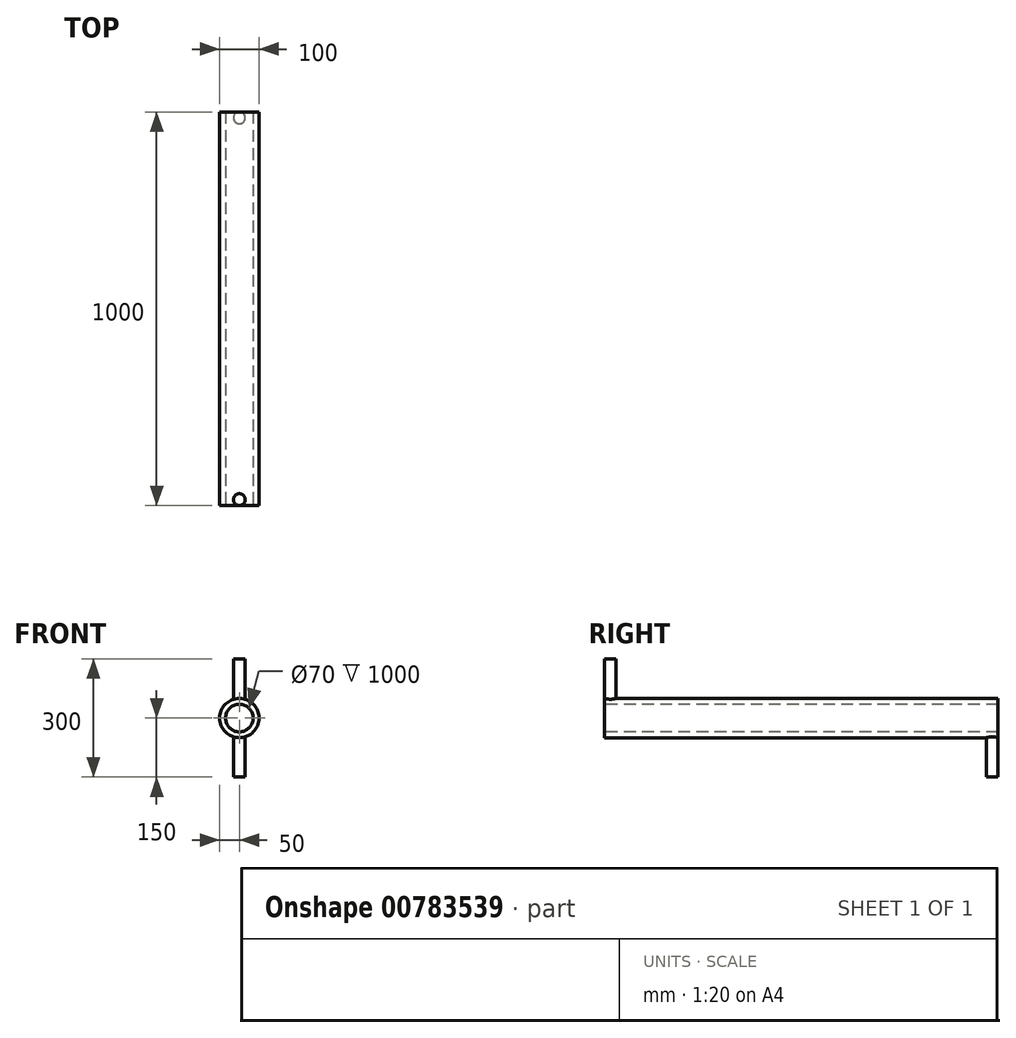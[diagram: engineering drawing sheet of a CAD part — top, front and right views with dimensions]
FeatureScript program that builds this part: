
annotation { "Feature Type Name" : "Feature", "Feature Type Description" : "" }
export const myFeature = defineFeature(function(context is Context, id is Id, definition is map)
    precondition{}
    {
        {
            var Q0;
            Q0=qCreatedBy(makeId("Front.planeOp"),FACE);
            var sketch = newSketch(context, id + "F0", { "sketchPlane" : qUnion([Q0])});
            skCircle(sketch, "E0", {"center": v(0, 0) * mm, "radius": 50 * mm});
            skCircle(sketch, "E1", {"center": v(0, 0) * mm, "radius": 35 * mm});
            skSolve(sketch);
        }
        {
            var Q0;
            Q0=makeQuery(id+"F0.imprint","IMPRINT",FACE,{"disambiguationData":[TD([[makeQuery(id+"F0.imprint","IMPRINT",EDGE,{"derivedFrom":sQuery(id+"F0.wireOp",EDGE,"E0")}),1.0]])]});
            extrude(context, id + "F1", {"entities" : qUnion([Q0]), "oppositeDirection" : true, "depth" : 1000 * mm, "offsetDistance" : 25 * mm});
        }
        {
            var Q0;
            Q0=qCreatedBy(makeId("Top.planeOp"),FACE);
            var sketch = newSketch(context, id + "F2", { "sketchPlane" : qUnion([Q0])});
            skCircle(sketch, "E2", {"center": v(0, 15) * mm, "radius": 15 * mm});
            skSolve(sketch);
        }
        {
            var Q0;
            Q0 = qSketchRegion(id + "F2", true);
            var Q1;
            Q1=makeQuery(id+"F1.opExtrude","SWEPT_FACE",FACE,{"disambiguationData":[OSD([sQuery(id+"F0.wireOp",EDGE,"E0")])]});
            extrude(context, id + "F3", {"entities" : qUnion([Q0]), "operationType" : NewBodyOperationType.ADD, "depth" : 150 * mm, "offsetDistance" : 25 * mm, "hasSecondDirection" : true, "secondDirectionBound" : SecondDirectionBoundingType.UP_TO_SURFACE, "secondDirectionOppositeDirection" : false, "secondDirectionDepth" : 25 * mm, "secondDirectionBoundEntityFace" : qUnion([Q1]), "hasSecondDirectionOffset" : true, "secondDirectionOffsetDistance" : 0 * mm, "secondDirectionOffsetOppositeDirection" : true});
        }
        {
            var Q0;
            Q0=qCreatedBy(makeId("Top.planeOp"),FACE);
            var sketch = newSketch(context, id + "F4", { "sketchPlane" : qUnion([Q0])});
            skCircle(sketch, "E3", {"center": v(0, 985) * mm, "radius": 15 * mm});
            skSolve(sketch);
        }
        {
            var Q0;
            Q0 = qSketchRegion(id + "F4", true);
            var Q1;
            Q1=makeQuery(id+"F1.opExtrude","SWEPT_FACE",FACE,{"disambiguationData":[OSD([sQuery(id+"F0.wireOp",EDGE,"E0")])]});
            extrude(context, id + "F5", {"entities" : qUnion([Q0]), "operationType" : NewBodyOperationType.ADD, "oppositeDirection" : true, "depth" : 150 * mm, "offsetDistance" : 25 * mm, "hasSecondDirection" : true, "secondDirectionBound" : SecondDirectionBoundingType.UP_TO_SURFACE, "secondDirectionOppositeDirection" : true, "secondDirectionDepth" : 25 * mm, "secondDirectionBoundEntityFace" : qUnion([Q1]), "hasSecondDirectionOffset" : true, "secondDirectionOffsetDistance" : 0 * mm});
        }
    });
